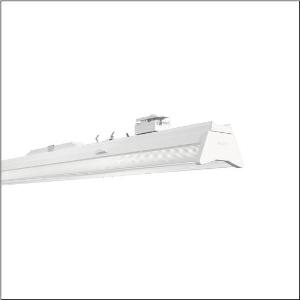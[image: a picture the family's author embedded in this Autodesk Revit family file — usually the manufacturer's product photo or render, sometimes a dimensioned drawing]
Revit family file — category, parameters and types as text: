
# Revit family: licross_r__21_performance_mo_52tm167n445g_e37c
name_source: partatom
category: Lighting Fixtures
units: mm (PartAtom-declared; Revit-internal decimal feet)

## family parameters
Cut with Voids When Loaded = No
Host = Face
Light Source = No
Part Type = Normal
Room Calculation Point = No
Round Connector Dimension = Use Diameter
Shared = No

## types (1)
- Licross® 21 Performance MO (1 x LED, 4580 lm, 24.7 W, 4000K)
    Apparent Load = 25 VA
    CIE Flux Codes = 66 88 96 79 100
    Color Rendering = 80
    Color Temperature = 4000K
    Default Elevation = 1800 mm
    Description = Licross® 21 Performance MO, luminaire insert, of sheet steel, galvanised, coil coated, white, length: 1.500mm, width: 120mm, height: 123mm, LED rated luminous flux: 4.580lm, light colour: 840, control gear: ON/OFF, with plug, 3-pole, with phase selection, mains connection: 220..240V, AC, 50/60Hz, rated input power: 25W, halogen-free wiring, primary light control with lens, of plastic, primary optical cover: cover, of PMMA, CAT 2 (L<= 3000cd/m²), light emission: direct/indirect distribution, primary light characteristic: symmetric, protection rating (complete): IP40, insulation class (complete): insulation class I (protective earthing), certification: CE, ENEC, UKCA, protection symbol: D if used in an environment without relevant dust loads with corresponding accessories, impact resistance: IK06, permissible ambient temperature for indoor applications: -35..+55°C, corresponds to IFS (International Featured Standards) requirements for safety and quality in the food industry, reducing of maximum allowable ambient temperature of 5°C with ceiling mounting, LABS conformity tested according to VDMA 24364:2018-05, packaging unit: 1 piece
    Height = 114 mm
    Lamp = 1 x LED
    Lamp Light Flux = 4580 lm
    Lamp Power = 24.7 W
    Lamp count = 1
    Length = 1500 mm
    Luminous efficacy = 185 lm/W
    Manufacturer = Siteco
    ModVariant = No
    Model = 52TM167N445G
    Mounting Place = Ceiling
    Mounting Type = Pendant
    Number of Poles = 1
    OnlyDefault = Yes
    Power Factor = 1
    Product Name = Licross® 21 Performance MO
    Product group = luminaire insert
    ProductGroupID = 901
    Protection Class = Protection class I
    Protection Degree = IP 40
    RLX_Detail_Level = 1
    RLX_Emergency_Light_Flux = 0 lm
    RLX_Emergency_Type = 0
    RLX_Emergency_Type_DB = No
    RlxData = <blob elided: 30449 chars, md5=aa896b1a>
    Socket = socket
    Standby Power = 0 W
    System Light Flux = 4580 lm
    System Power = 25 W
    Type Comments = Product without accessories
    Type Image = l_1256138.jpg
    URL = http://relux.com
    VarID = ---
    Voltage = 0 V
    Weight = 0.00 kg
    Width = 120 mm

## geometry (parser evidence)
native form markers: Blend x4, Sweep x11
no freeform markers — native parametric forms only
